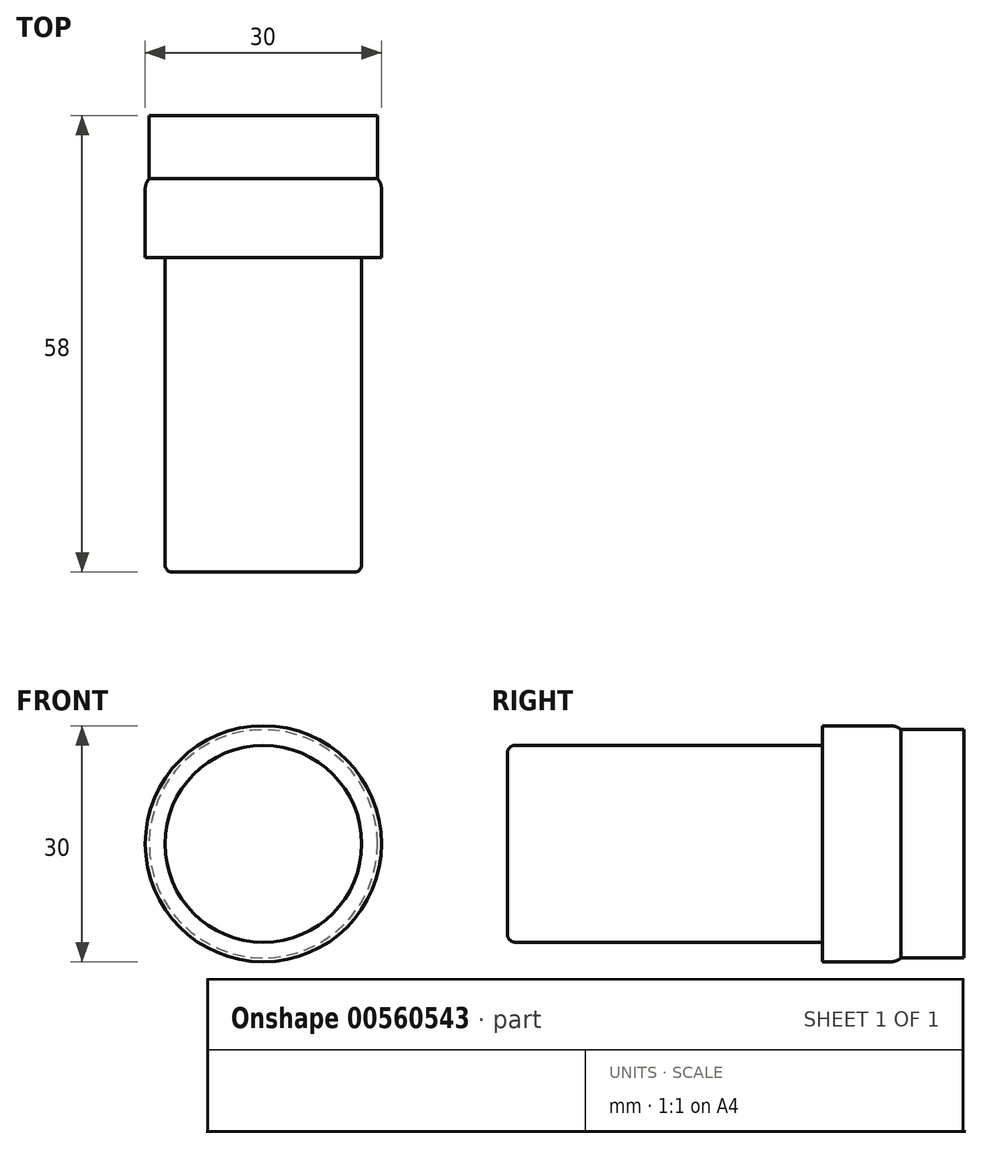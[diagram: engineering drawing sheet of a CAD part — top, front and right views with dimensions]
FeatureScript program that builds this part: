
annotation { "Feature Type Name" : "Feature", "Feature Type Description" : "" }
export const myFeature = defineFeature(function(context is Context, id is Id, definition is map)
    precondition{}
    {
        {
            var Q0;
            Q0=qCreatedBy(makeId("Front.planeOp"),FACE);
            var sketch = newSketch(context, id + "F0", { "sketchPlane" : qUnion([Q0])});
            skCircle(sketch, "E0", {"center": v(-53.26, 6.23) * mm, "radius": 15 * mm});
            skSolve(sketch);
        }
        {
            var Q0;
            Q0=makeQuery(id+"F0.imprint","IMPRINT",FACE,{"disambiguationData":[TD([[makeQuery(id+"F0.imprint","IMPRINT",EDGE,{"derivedFrom":sQuery(id+"F0.wireOp",EDGE,"E0")}),1.0]])]});
            extrude(context, id + "F1", {"entities" : qUnion([Q0]), "depth" : 10 * mm, "offsetDistance" : 25 * mm});
        }
        {
            var Q0;
            Q0=makeQuery(id+"F1.opExtrude","CAP_FACE",FACE,{"disambiguationData":[OSD([sQuery(id+"F0.wireOp",EDGE,"E0")])],"isStart":false});
            var sketch = newSketch(context, id + "F2", { "sketchPlane" : qUnion([Q0])});
            skCircle(sketch, "E1", {"center": v(-53.26, 6.23) * mm, "radius": 12.5 * mm});
            skSolve(sketch);
        }
        {
            var Q0;
            Q0=makeQuery(id+"F2.imprint","IMPRINT",FACE,{"disambiguationData":[TD([[makeQuery(id+"F2.imprint","IMPRINT",EDGE,{"derivedFrom":sQuery(id+"F2.wireOp",EDGE,"E1")}),1.0]])]});
            extrude(context, id + "F3", {"entities" : qUnion([Q0]), "operationType" : NewBodyOperationType.ADD, "depth" : 40 * mm, "offsetDistance" : 25 * mm});
        }
        {
            var Q0;
            Q0=makeQuery(id+"F3.opExtrude","CAP_EDGE",EDGE,{"disambiguationData":[OSD([sQuery(id+"F2.wireOp",EDGE,"E1")])],"isStart":false});
            fillet(context, id + "F4", {"entities" : qUnion([Q0]), "radius" : 1 * mm, "tangentPropagation" : true, "allowEdgeOverflow" : false});
        }
        {
            var Q0;
            Q0=makeQuery(id+"F1.opExtrude","CAP_FACE",FACE,{"disambiguationData":[OSD([sQuery(id+"F0.wireOp",EDGE,"E0")])],"isStart":true});
            var sketch = newSketch(context, id + "F5", { "sketchPlane" : qUnion([Q0])});
            skCircle(sketch, "E2", {"center": v(53.26, 6.23) * mm, "radius": 14.5 * mm});
            skSolve(sketch);
        }
        {
            var Q0;
            Q0=makeQuery(id+"F5.imprint","IMPRINT",FACE,{"disambiguationData":[TD([[makeQuery(id+"F5.imprint","IMPRINT",EDGE,{"derivedFrom":sQuery(id+"F5.wireOp",EDGE,"E2")}),1.0]])]});
            extrude(context, id + "F6", {"entities" : qUnion([Q0]), "operationType" : NewBodyOperationType.ADD, "depth" : 8 * mm, "offsetDistance" : 25 * mm});
        }
        {
            var Q0;
            Q0=makeQuery(id+"F1.opExtrude","CAP_EDGE",EDGE,{"disambiguationData":[OSD([sQuery(id+"F0.wireOp",EDGE,"E0")])],"isStart":true});
            fillet(context, id + "F7", {"entities" : qUnion([Q0]), "radius" : 2 * mm, "tangentPropagation" : true, "allowEdgeOverflow" : false});
        }
    });
